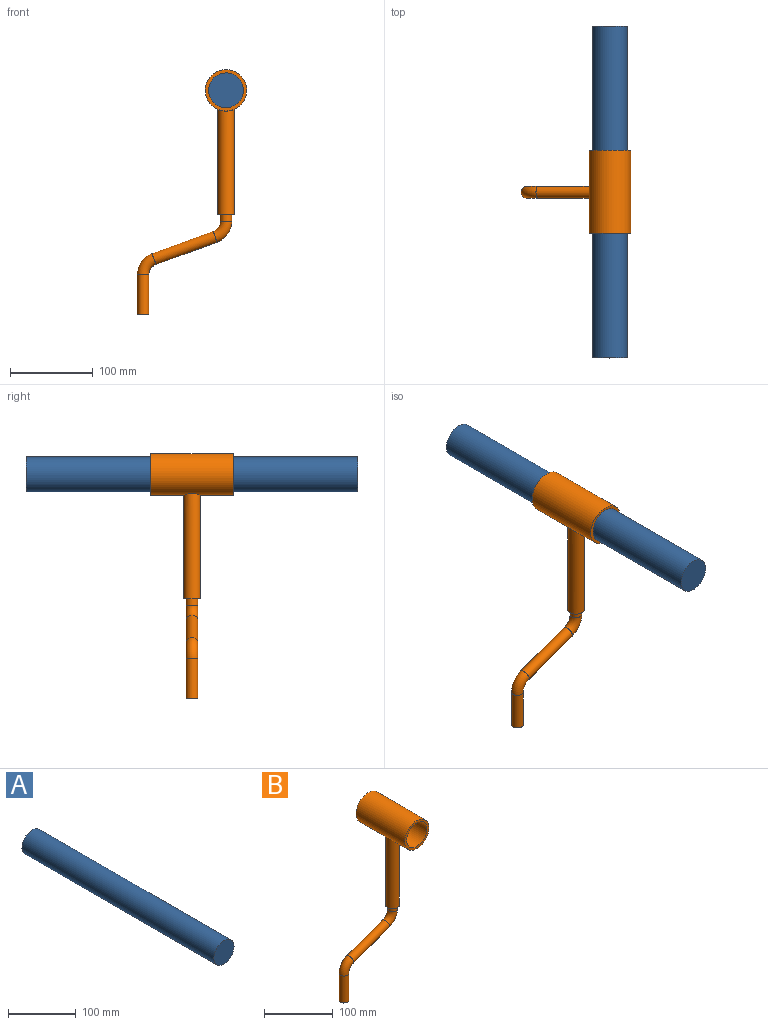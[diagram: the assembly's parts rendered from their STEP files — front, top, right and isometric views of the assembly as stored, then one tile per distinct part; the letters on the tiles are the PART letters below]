
ASSEMBLY  parts=2 mates=1
PART A: 3 faces, bbox 42x400x42 mm
  f0: cylinder r=21mm len=400mm, axis (0,1,0), area 52778.8mm2, adj f1,f2
  f1: plane 42x42mm, normal (0,-1,0), area 1385.4mm2, adj f0
  f2: plane 42x42mm, normal (0,1,0), area 1385.4mm2, adj f0
PART B: 15 faces, bbox 134.2x100x295 mm
  f0: cylinder r=10mm len=127.09mm, axis (0,0,-1), area 7918.7mm2, adj f7,f10
  f1: plane 14x14mm, normal (0,0,-1), area 153.9mm2, adj f2
  f2: cylinder r=7mm len=48mm, axis (0,0,1), area 2111.2mm2, adj f1,f3
  f3: torus R=20mm, axis (0,1,0), area 1074.7mm2, adj f2,f4
  f4: cylinder r=7mm len=78.47mm, axis (0.94,0,0.34), area 3448.6mm2, adj f3,f5
  f5: torus R=20mm, axis (0,-1,0), area 1074.7mm2, adj f4,f6
  f6: cylinder r=7mm len=14mm, axis (0,0,1), area 334mm2, adj f5,f7
  f7: plane 20x20mm, normal (0,0,-1), area 160.2mm2, adj f0,f6
  f8: plane 50x50mm, normal (0,1,0), area 578.1mm2, adj f10,f11
  f9: plane 50x50mm, normal (0,-1,0), area 578.1mm2, adj f10,f11
  f10: cylinder r=25mm len=100mm, axis (0,1,0), area 15387.2mm2, adj f0,f8,f9
  f11: cylinder r=21mm len=100mm, axis (0,1,0), area 13194.7mm2, adj f8,f9
  f12: plane 14x14mm, normal (0,0,1), area 153.9mm2, adj f13
  f13: cylinder r=7mm len=76mm, axis (0,0,-1), area 3320.6mm2, adj f12,f14
  f14: cylinder r=25mm len=14mm, axis (0,1,0), area 155.5mm2, adj f13
PLACE A rot(axis=(0,0,1),0deg) t=(1468,0,0)mm
PLACE B rot(axis=(0,0,1),0deg) t=(1468,0,0)mm
MATE fastened A.f0 <-> B.f10  axis (0,1,0) through (0,0,226)mm
